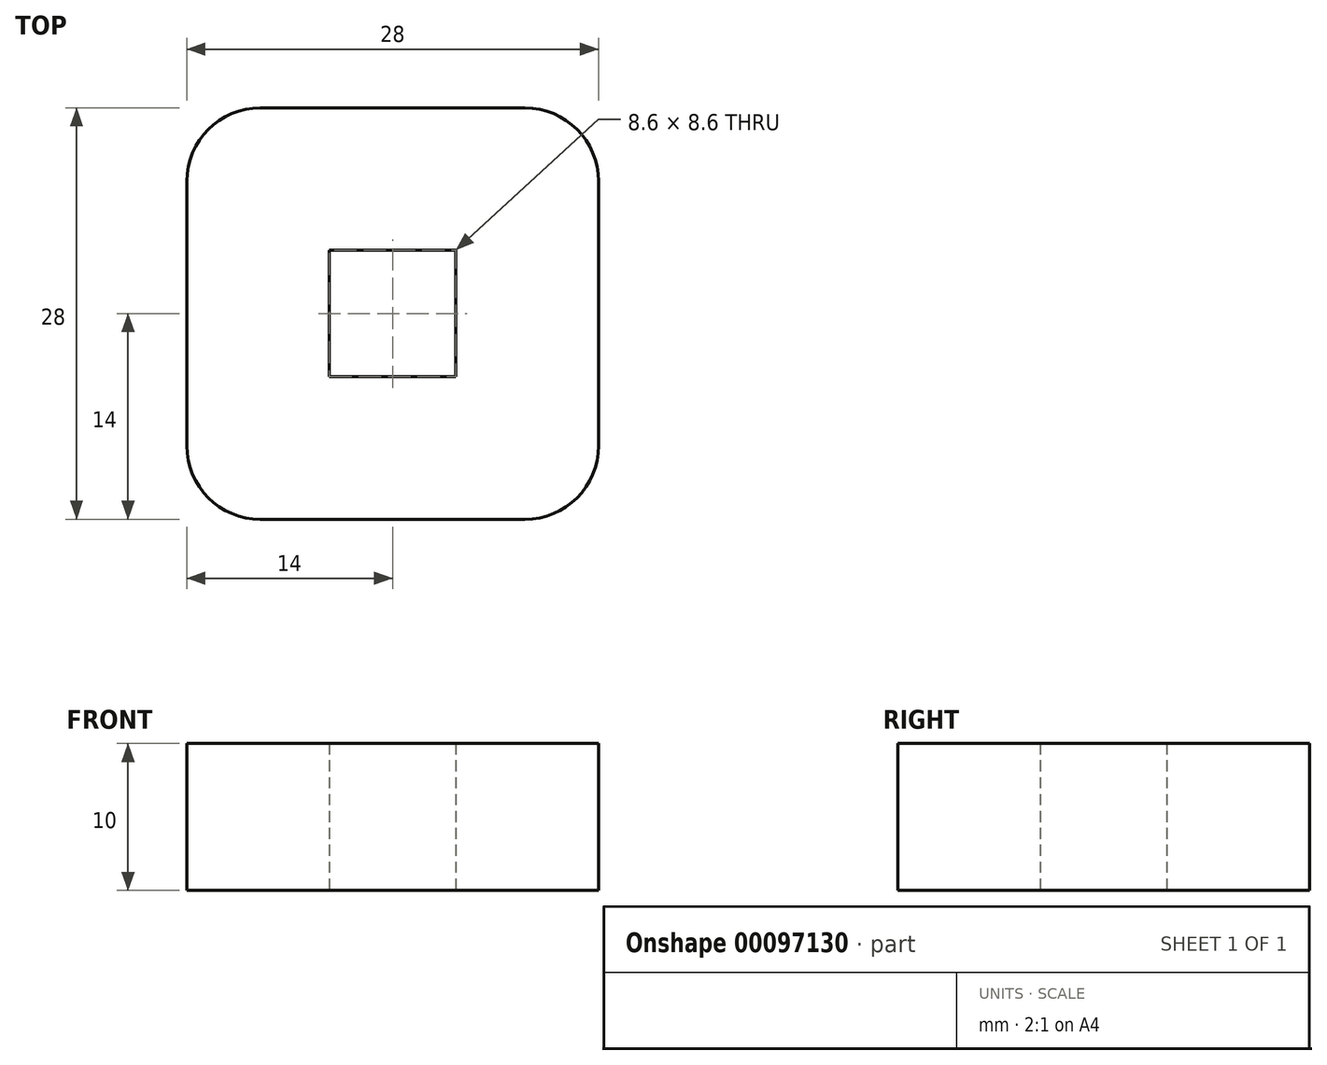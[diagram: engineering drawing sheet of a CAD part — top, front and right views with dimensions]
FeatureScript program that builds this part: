
annotation { "Feature Type Name" : "Feature", "Feature Type Description" : "" }
export const myFeature = defineFeature(function(context is Context, id is Id, definition is map)
    precondition{}
    {
        {
            var Q0;
            Q0=qCreatedBy(makeId("Top.planeOp"),FACE);
            var sketch = newSketch(context, id + "F0", { "sketchPlane" : qUnion([Q0])});
            skLineSegment(sketch, "E0.bottom", {"start": v(0, 0) * mm, "end": v(28, 0) * mm});
            skLineSegment(sketch, "E0.top", {"start": v(0, 28) * mm, "end": v(28, 28) * mm});
            skLineSegment(sketch, "E0.left", {"start": v(0, 0) * mm, "end": v(0, 28) * mm});
            skLineSegment(sketch, "E0.right", {"start": v(28, 0) * mm, "end": v(28, 28) * mm});
            skLineSegment(sketch, "E1", {"start": v(14, 28) * mm, "end": v(14, 0) * mm, "construction": true});
            skLineSegment(sketch, "E2.bottom", {"start": v(9.7, 18.3) * mm, "end": v(18.3, 18.3) * mm});
            skLineSegment(sketch, "E2.top", {"start": v(9.7, 9.7) * mm, "end": v(18.3, 9.7) * mm});
            skLineSegment(sketch, "E2.left", {"start": v(9.7, 18.3) * mm, "end": v(9.7, 9.7) * mm});
            skLineSegment(sketch, "E2.right", {"start": v(18.3, 18.3) * mm, "end": v(18.3, 9.7) * mm});
            skPoint(sketch, "E2.middle", {"position": v(14, 14) * mm});
            skSolve(sketch);
        }
        {
            var Q0;
            Q0 = qSketchRegion(id + "F0", true);
            extrude(context, id + "F1", {"entities" : qUnion([Q0]), "depth" : 10 * mm});
        }
        {
            var Q0;
            Q0=makeQuery(id+"F1.opExtrude","SWEPT_EDGE",EDGE,{"disambiguationData":[OSD([sQuery(id+"F0.wireOp",EDGE,"E0.bottom"),sQuery(id+"F0.wireOp",EDGE,"E0.left")])]});
            var Q1;
            Q1=makeQuery(id+"F1.opExtrude","SWEPT_EDGE",EDGE,{"disambiguationData":[OSD([sQuery(id+"F0.wireOp",EDGE,"E0.bottom"),sQuery(id+"F0.wireOp",EDGE,"E0.right")])]});
            var Q2;
            Q2=makeQuery(id+"F1.opExtrude","SWEPT_EDGE",EDGE,{"disambiguationData":[OSD([sQuery(id+"F0.wireOp",EDGE,"E0.top"),sQuery(id+"F0.wireOp",EDGE,"E0.right")])]});
            var Q3;
            Q3=makeQuery(id+"F1.opExtrude","SWEPT_EDGE",EDGE,{"disambiguationData":[OSD([sQuery(id+"F0.wireOp",EDGE,"E0.top"),sQuery(id+"F0.wireOp",EDGE,"E0.left")])]});
            fillet(context, id + "F2", {"entities" : qUnion([Q0, Q1, Q2, Q3]), "radius" : 5 * mm, "tangentPropagation" : true, "allowEdgeOverflow" : false});
        }
    });
